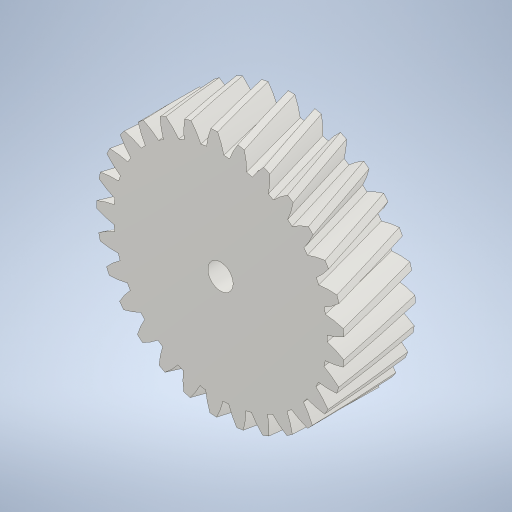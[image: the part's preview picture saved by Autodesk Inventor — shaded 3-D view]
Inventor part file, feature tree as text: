
AUTODESK INVENTOR PART (.ipt)
format: ipt  version: 2024.1 (Build 281209000, 209)  size: 608,256 bytes
history: native  units: mm (DEFAULTED — no unit token found)
features: plane x3, other x3, extrude x2, sketch x2
ambient origin geometry x8: Origin, YZ Plane, XZ Plane, XY Plane, X Axis, Y Axis, Z Axis, Center Point
bodies: Solid1 (feature_tree)
feature tree (10):
  extrude  "Extrusion1"  Depth=14.0mm TaperAngle=0.0deg
  plane  "Work Plane2"
  plane  "Work Plane8"
  plane  "Work Plane9"
  other  "Spur Gear"
  extrude  "Extrusion2"  Depth=10.0mm TaperAngle=0.0deg
  sketch  "Sketch1"  dims[d0=48.837039mm d1=14.0mm d2=0.0mm]
  other  "Srf1"
  sketch  "Sketch3"  dims[d3=45.034514mm d4=10.0mm d5=0.0mm d16=45.0mm d17=0.0mm d34=1.083308mm d39=0.0mm d41=0.0mm d43=45.0mm d46=45.0mm d47=0.0mm d48=0.0mm d49=5.0mm d50=0.0mm d51=0.0mm]
  other  "Pitch Diameter"
